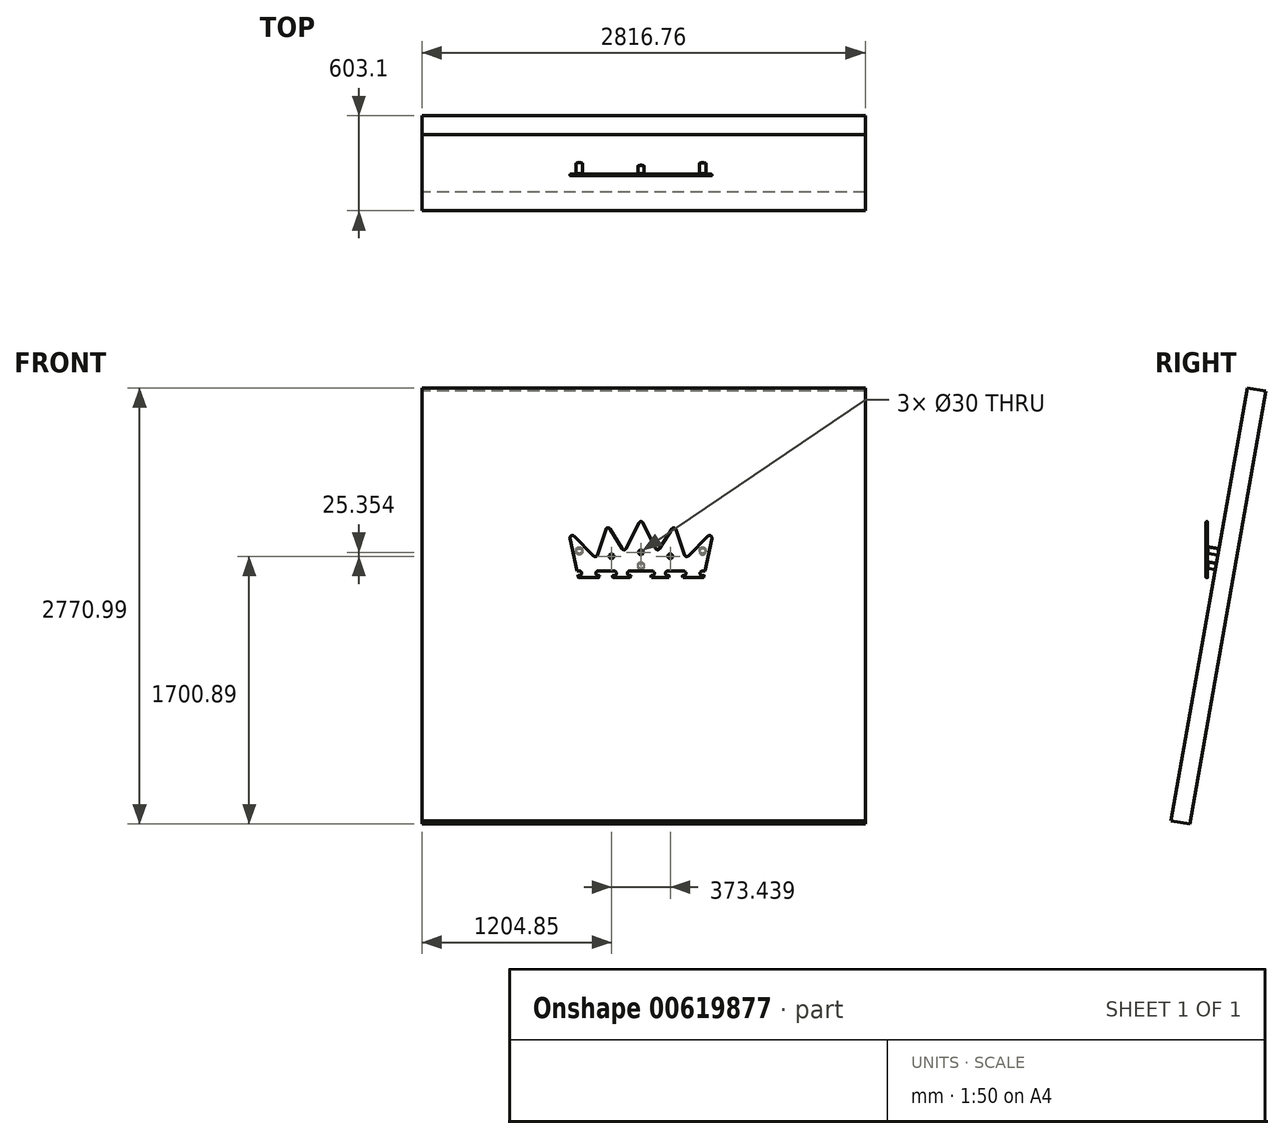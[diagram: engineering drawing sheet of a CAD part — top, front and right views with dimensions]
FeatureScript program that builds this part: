
annotation { "Feature Type Name" : "Feature", "Feature Type Description" : "" }
export const myFeature = defineFeature(function(context is Context, id is Id, definition is map)
    precondition{}
    {
        {
            var Q0;
            Q0=qCreatedBy(makeId("Front.planeOp"),FACE);
            var sketch = newSketch(context, id + "F0", { "sketchPlane" : qUnion([Q0])});
            skLineSegment(sketch, "E0.left", {"start": v(0, 0) * mm, "end": v(0, 300) * mm, "construction": true});
            skLineSegment(sketch, "E1", {"start": v(0, 0) * mm, "end": v(-52.87, 249.42) * mm});
            skLineSegment(sketch, "E2", {"start": v(-27.53, 263.07) * mm, "end": v(113.33, 120.6) * mm});
            skLineSegment(sketch, "E3", {"start": v(0, 35) * mm, "end": v(1158.58, 35) * mm, "construction": true});
            skArc(sketch, "E4.filletArc", {"start": v(-27.53, 263.07) * mm, "mid": v(-45.3, 265.73) * mm, "end": v(-52.87, 249.42) * mm});
            skLineSegment(sketch, "E5", {"start": v(397.13, 374.35) * mm, "end": v(397.13, 0) * mm});
            skLineSegment(sketch, "E6", {"start": v(0, 0) * mm, "end": v(397.13, 0) * mm});
            skLineSegment(sketch, "E7", {"start": v(113.33, 120.6) * mm, "end": v(184.19, 337.1) * mm});
            skLineSegment(sketch, "E8", {"start": v(184.19, 337.1) * mm, "end": v(291.92, 160.57) * mm});
            skLineSegment(sketch, "E9", {"start": v(291.92, 160.57) * mm, "end": v(397.13, 374.35) * mm});
            skSolve(sketch);
        }
        {
            var Q0;
            Q0=makeQuery(id+"F0.imprint","IMPRINT",FACE,{"disambiguationData":[TD([[makeQuery(id+"F0.imprint","IMPRINT",EDGE,{"derivedFrom":sQuery(id+"F0.wireOp",EDGE,"E1")}),-1.0]])]});
            extrude(context, id + "F1", {"entities" : qUnion([Q0]), "depth" : 9 * mm, "offsetDistance" : 25 * mm});
        }
        {
            var Q0;
            Q0=makeQuery(id+"F1.opExtrude","SWEPT_EDGE",EDGE,{"disambiguationData":[OSD([sQuery(id+"F0.wireOp",EDGE,"E2"),sQuery(id+"F0.wireOp",EDGE,"E7")])]});
            var Q1;
            Q1=makeQuery(id+"F1.opExtrude","SWEPT_EDGE",EDGE,{"disambiguationData":[OSD([sQuery(id+"F0.wireOp",EDGE,"E7"),sQuery(id+"F0.wireOp",EDGE,"E8")])]});
            var Q2;
            Q2=makeQuery(id+"F1.opExtrude","SWEPT_EDGE",EDGE,{"disambiguationData":[OSD([sQuery(id+"F0.wireOp",EDGE,"E8"),sQuery(id+"F0.wireOp",EDGE,"E9")])]});
            fillet(context, id + "F2", {"entities" : qUnion([Q0, Q1, Q2]), "radius" : 15 * mm, "tangentPropagation" : true, "allowEdgeOverflow" : false});
        }
        {
            var Q0;
            Q0=makeQuery(id+"F1.opExtrude","CAP_FACE",FACE,{"disambiguationData":[OSD([sQuery(id+"F0.wireOp",EDGE,"E1"),sQuery(id+"F0.wireOp",EDGE,"E2"),sQuery(id+"F0.wireOp",EDGE,"E4.filletArc"),sQuery(id+"F0.wireOp",EDGE,"E5"),sQuery(id+"F0.wireOp",EDGE,"E6"),sQuery(id+"F0.wireOp",EDGE,"E7"),sQuery(id+"F0.wireOp",EDGE,"E8"),sQuery(id+"F0.wireOp",EDGE,"E9")])],"isStart":false});
            var sketch = newSketch(context, id + "F3", { "sketchPlane" : qUnion([Q0])});
            skCircle(sketch, "E10", {"center": v(6.24, 27) * mm, "radius": 15 * mm});
            skLineSegment(sketch, "E11", {"start": v(6.24, 42) * mm, "end": v(-8.9, 42) * mm});
            skSolve(sketch);
        }
        {
            var Q0;
            {var subQ0=sQuery(id+"F3.wireOp",EDGE,"E10");var subQ1=makeQuery(id+"F3.imprint","INTERSECT",VERTEX,{"derivedFrom":[subQ0,sQuery(id+"F3.wireOp",EDGE,"E11")]});Q0=makeQuery(id+"F3.imprint","IMPRINT",FACE,{"disambiguationData":[TD([[makeQuery(id+"F3.imprint","IMPRINT",EDGE,{"disambiguationData":[TD([[subQ1,-1.0]])],"derivedFrom":subQ0}),1.0]])]});}
            var Q1;
            {var subQ0=sQuery(id+"F3.wireOp",EDGE,"E11");Q1=makeQuery(id+"F3.imprint","IMPRINT",FACE,{"disambiguationData":[TD([[makeQuery(id+"F3.imprint","IMPRINT",EDGE,{"derivedFrom":subQ0}),1.0]])]});}
            extrude(context, id + "F4", {"entities" : qUnion([Q0, Q1]), "operationType" : NewBodyOperationType.REMOVE, "endBound" : BoundingType.THROUGH_ALL, "oppositeDirection" : true, "depth" : 25 * mm, "offsetDistance" : 25 * mm});
        }
        {
            var Q0;
            Q0=makeQuery(id+"F1.opExtrude","CAP_FACE",FACE,{"disambiguationData":[OSD([sQuery(id+"F0.wireOp",EDGE,"E1"),sQuery(id+"F0.wireOp",EDGE,"E2"),sQuery(id+"F0.wireOp",EDGE,"E4.filletArc"),sQuery(id+"F0.wireOp",EDGE,"E5"),sQuery(id+"F0.wireOp",EDGE,"E6"),sQuery(id+"F0.wireOp",EDGE,"E7"),sQuery(id+"F0.wireOp",EDGE,"E8"),sQuery(id+"F0.wireOp",EDGE,"E9")])],"isStart":false});
            var sketch = newSketch(context, id + "F5", { "sketchPlane" : qUnion([Q0])});
            skCircle(sketch, "E12", {"center": v(126.24, 27) * mm, "radius": 15 * mm});
            skLineSegment(sketch, "E13", {"start": v(6.24, 27) * mm, "end": v(126.24, 27) * mm, "construction": true});
            skCircle(sketch, "E14.1.0.0", {"center": v(226.24, 27) * mm, "radius": 15 * mm});
            skCircle(sketch, "E14.2.0.0", {"center": v(326.24, 27) * mm, "radius": 15 * mm});
            skLineSegment(sketch, "E14.direction1", {"start": v(126.24, 27) * mm, "end": v(226.24, 27) * mm, "construction": true});
            skLineSegment(sketch, "E15", {"start": v(126.24, 42) * mm, "end": v(226.24, 42) * mm});
            skLineSegment(sketch, "E16", {"start": v(-3.26, 15.4) * mm, "end": v(135.75, 15.4) * mm, "construction": true});
            skLineSegment(sketch, "E17", {"start": v(135.75, 15.4) * mm, "end": v(216.74, 15.4) * mm, "construction": true});
            skLineSegment(sketch, "E18", {"start": v(326.24, 42) * mm, "end": v(397.13, 42) * mm});
            skLineSegment(sketch, "E19", {"start": v(335.75, 15.4) * mm, "end": v(397.13, 16.4) * mm, "construction": true});
            skLineSegment(sketch, "E20", {"start": v(135.75, 15.4) * mm, "end": v(129.34, 0) * mm});
            skLineSegment(sketch, "E21", {"start": v(216.74, 15.4) * mm, "end": v(220, 0) * mm});
            skLineSegment(sketch, "E22", {"start": v(335.75, 15.4) * mm, "end": v(329.34, 0) * mm});
            skSolve(sketch);
        }
        {
            var Q0;
            {var subQ0=sQuery(id+"F5.wireOp",EDGE,"E12");var subQ1=makeQuery(id+"F5.imprint","INTERSECT",VERTEX,{"derivedFrom":[subQ0,sQuery(id+"F5.wireOp",EDGE,"E15")]});Q0=makeQuery(id+"F5.imprint","IMPRINT",FACE,{"disambiguationData":[TD([[makeQuery(id+"F5.imprint","IMPRINT",EDGE,{"disambiguationData":[TD([[subQ1,-1.0]])],"derivedFrom":subQ0}),1.0]])]});}
            var Q1;
            {var subQ1=sQuery(id+"F5.wireOp",EDGE,"E15");Q1=makeQuery(id+"F5.imprint","IMPRINT",FACE,{"disambiguationData":[TD([[makeQuery(id+"F5.imprint","IMPRINT",EDGE,{"derivedFrom":subQ1}),-1.0]])]});}
            var Q2;
            {var subQ0=sQuery(id+"F5.wireOp",EDGE,"E14.1.0.0");var subQ1=makeQuery(id+"F5.imprint","INTERSECT",VERTEX,{"derivedFrom":[subQ0,sQuery(id+"F5.wireOp",EDGE,"E15")]});Q2=makeQuery(id+"F5.imprint","IMPRINT",FACE,{"disambiguationData":[TD([[makeQuery(id+"F5.imprint","IMPRINT",EDGE,{"disambiguationData":[TD([[subQ1,-1.0]])],"derivedFrom":subQ0}),1.0]])]});}
            var Q3;
            {var subQ0=sQuery(id+"F5.wireOp",EDGE,"E14.2.0.0");var subQ1=makeQuery(id+"F5.imprint","INTERSECT",VERTEX,{"derivedFrom":[subQ0,sQuery(id+"F5.wireOp",EDGE,"E18")]});Q3=makeQuery(id+"F5.imprint","IMPRINT",FACE,{"disambiguationData":[TD([[makeQuery(id+"F5.imprint","IMPRINT",EDGE,{"disambiguationData":[TD([[subQ1,-1.0]])],"derivedFrom":subQ0}),1.0]])]});}
            var Q4;
            {var subQ3=sQuery(id+"F5.wireOp",EDGE,"E18");Q4=makeQuery(id+"F5.imprint","IMPRINT",FACE,{"disambiguationData":[TD([[makeQuery(id+"F5.imprint","IMPRINT",EDGE,{"derivedFrom":subQ3}),-1.0]])]});}
            extrude(context, id + "F6", {"entities" : qUnion([Q0, Q1, Q2, Q3, Q4]), "operationType" : NewBodyOperationType.REMOVE, "endBound" : BoundingType.THROUGH_ALL, "oppositeDirection" : true, "depth" : 25 * mm, "offsetDistance" : 25 * mm});
        }
        {
            var Q0;
            Q0=makeQuery(id+"F4.boolean.opBoolean","COPY",EDGE,{"derivedFrom":makeQuery(id+"F4.opExtrude","SWEPT_EDGE",EDGE,{"disambiguationData":[OSD([sQuery(id+"F0.wireOp",EDGE,"E1"),sQuery(id+"F3.wireOp",EDGE,"E10")])]})});
            var Q1;
            Q1=makeQuery(id+"F1.opExtrude","SWEPT_EDGE",EDGE,{"disambiguationData":[OSD([sQuery(id+"F0.wireOp",EDGE,"E1"),sQuery(id+"F0.wireOp",EDGE,"E6")])]});
            var Q2;
            Q2=makeQuery(id+"F6.boolean.opBoolean","COPY",EDGE,{"derivedFrom":makeQuery(id+"F6.opExtrude","SWEPT_EDGE",EDGE,{"disambiguationData":[OSD([sQuery(id+"F5.wireOp",EDGE,"E12"),sQuery(id+"F5.wireOp",EDGE,"E20")])]})});
            var Q3;
            Q3=makeQuery(id+"F6.boolean.opBoolean","COPY",EDGE,{"derivedFrom":makeQuery(id+"F6.opExtrude","SWEPT_EDGE",EDGE,{"disambiguationData":[OSD([sQuery(id+"F0.wireOp",EDGE,"E6"),sQuery(id+"F5.wireOp",EDGE,"E20")])]})});
            var Q4;
            Q4=makeQuery(id+"F6.boolean.opBoolean","COPY",EDGE,{"derivedFrom":makeQuery(id+"F6.opExtrude","SWEPT_EDGE",EDGE,{"disambiguationData":[OSD([sQuery(id+"F5.wireOp",EDGE,"E14.2.0.0"),sQuery(id+"F5.wireOp",EDGE,"E22")])]})});
            var Q5;
            Q5=makeQuery(id+"F6.boolean.opBoolean","COPY",EDGE,{"derivedFrom":makeQuery(id+"F6.opExtrude","SWEPT_EDGE",EDGE,{"disambiguationData":[OSD([sQuery(id+"F0.wireOp",EDGE,"E6"),sQuery(id+"F5.wireOp",EDGE,"E22")])]})});
            var Q6;
            Q6=makeQuery(id+"F6.boolean.opBoolean","COPY",EDGE,{"derivedFrom":makeQuery(id+"F6.opExtrude","SWEPT_EDGE",EDGE,{"disambiguationData":[OSD([sQuery(id+"F0.wireOp",EDGE,"E6"),sQuery(id+"F5.wireOp",EDGE,"E21")])]})});
            var Q7;
            Q7=makeQuery(id+"F6.boolean.opBoolean","COPY",EDGE,{"derivedFrom":makeQuery(id+"F6.opExtrude","SWEPT_EDGE",EDGE,{"disambiguationData":[OSD([sQuery(id+"F5.wireOp",EDGE,"E14.1.0.0"),sQuery(id+"F5.wireOp",EDGE,"E21")])]})});
            fillet(context, id + "F7", {"entities" : qUnion([Q0, Q1, Q2, Q3, Q4, Q5, Q6, Q7]), "radius" : 2 * mm, "tangentPropagation" : true, "allowEdgeOverflow" : false});
        }
        {
            var Q0;
            Q0=makeQuery(id+"F1.opExtrude","CAP_FACE",FACE,{"disambiguationData":[OSD([sQuery(id+"F0.wireOp",EDGE,"E1"),sQuery(id+"F0.wireOp",EDGE,"E2"),sQuery(id+"F0.wireOp",EDGE,"E4.filletArc"),sQuery(id+"F0.wireOp",EDGE,"E5"),sQuery(id+"F0.wireOp",EDGE,"E6"),sQuery(id+"F0.wireOp",EDGE,"E7"),sQuery(id+"F0.wireOp",EDGE,"E8"),sQuery(id+"F0.wireOp",EDGE,"E9")])],"isStart":false});
            var sketch = newSketch(context, id + "F8", { "sketchPlane" : qUnion([Q0])});
            skCircle(sketch, "E23", {"center": v(210.41, 135.31) * mm, "radius": 15 * mm});
            skCircle(sketch, "E24", {"center": v(397.13, 160.66) * mm, "radius": 15 * mm});
            skSolve(sketch);
        }
        {
            var Q0;
            Q0=makeQuery(id+"F8.imprint","IMPRINT",FACE,{"disambiguationData":[TD([[makeQuery(id+"F8.imprint","IMPRINT",EDGE,{"derivedFrom":sQuery(id+"F8.wireOp",EDGE,"40AQ9wcr-OVRQ-jtMO-fQ6l-KvRctUFFu5MA")}),1.0]])]});
            var Q1;
            Q1=makeQuery(id+"F8.imprint","IMPRINT",FACE,{"disambiguationData":[TD([[makeQuery(id+"F8.imprint","IMPRINT",EDGE,{"derivedFrom":sQuery(id+"F8.wireOp",EDGE,"E23")}),1.0]])]});
            var Q2;
            {var subQ0=sQuery(id+"F8.wireOp",EDGE,"E24");var subQ1=makeQuery(id+"F1.opExtrude","CAP_EDGE",EDGE,{"disambiguationData":[OSD([sQuery(id+"F0.wireOp",EDGE,"E5")])],"isStart":false});var subQ2=makeQuery(id+"F8.imprint","INTERSECT",VERTEX,{"disambiguationData":[OD(0.0)],"derivedFrom":[subQ1,subQ0]});Q2=makeQuery(id+"F8.imprint","IMPRINT",FACE,{"disambiguationData":[TD([[makeQuery(id+"F8.imprint","IMPRINT",EDGE,{"disambiguationData":[TD([[subQ2,-1.0]])],"derivedFrom":subQ0}),1.0]])]});}
            extrude(context, id + "F9", {"entities" : qUnion([Q0, Q1, Q2]), "operationType" : NewBodyOperationType.REMOVE, "endBound" : BoundingType.THROUGH_ALL, "oppositeDirection" : true, "depth" : 25 * mm, "offsetDistance" : 25 * mm});
        }
        {
            var Q0;
            {var subQ0=sQuery(id+"F0.wireOp",EDGE,"E6");Q0=makeQuery(id+"F6.boolean.opBoolean","SPLIT",EDGE,{"disambiguationData":[TD([makeQuery(id+"F6.opExtrude","SWEPT_FACE",FACE,{"disambiguationData":[OSD([sQuery(id+"F5.wireOp",EDGE,"E21")])]})])],"derivedFrom":makeQuery(id+"F1.opExtrude","CAP_EDGE",EDGE,{"disambiguationData":[OSD([subQ0])],"isStart":true})});}
            cPlane(context, id + "F10", {"entities" : qUnion([Q0]), "cplaneType" : CPlaneType.LINE_ANGLE, "offset" : 25 * mm, "angle" : 10 * degree, "oppositeDirection" : true, "width" : 150 * mm, "height" : 150 * mm});
        }
        {
            var Q0;
            Q0=qCreatedBy(id+"F10.planeOp",FACE);
            cPlane(context, id + "F11", {"entities" : qUnion([Q0]), "cplaneType" : CPlaneType.OFFSET, "offset" : 40 * mm, "width" : 150 * mm, "height" : 150 * mm});
        }
        {
            var Q0;
            Q0=qCreatedBy(id+"F11.planeOp",FACE);
            var sketch = newSketch(context, id + "F12", { "sketchPlane" : qUnion([Q0])});
            skCircle(sketch, "E25", {"center": v(-5.4, 172.6) * mm, "radius": 20 * mm});
            skCircle(sketch, "E26", {"center": v(-397.13, 78.47) * mm, "radius": 20 * mm});
            skSolve(sketch);
        }
        {
            var Q0;
            Q0=makeQuery(id+"F12.imprint","IMPRINT",FACE,{"disambiguationData":[TD([[makeQuery(id+"F12.imprint","IMPRINT",EDGE,{"derivedFrom":sQuery(id+"F12.wireOp",EDGE,"E26")}),1.0]])]});
            var Q1;
            Q1=makeQuery(id+"F12.imprint","IMPRINT",FACE,{"disambiguationData":[TD([[makeQuery(id+"F12.imprint","IMPRINT",EDGE,{"derivedFrom":sQuery(id+"F12.wireOp",EDGE,"E25")}),1.0]])]});
            var Q2;
            {var subQ0=makeQuery(id+"F1.opExtrude","CAP_FACE",FACE,{"disambiguationData":[OSD([sQuery(id+"F0.wireOp",EDGE,"E1"),sQuery(id+"F0.wireOp",EDGE,"E2"),sQuery(id+"F0.wireOp",EDGE,"E4.filletArc"),sQuery(id+"F0.wireOp",EDGE,"E5"),sQuery(id+"F0.wireOp",EDGE,"E6"),sQuery(id+"F0.wireOp",EDGE,"E7"),sQuery(id+"F0.wireOp",EDGE,"E8"),sQuery(id+"F0.wireOp",EDGE,"E9")])],"isStart":true});Q2=makeQuery(id+"F15.boolean.opBoolean","MERGE",FACE,{"derivedFrom":[subQ0,makeQuery(id+"F15.opPattern","COPY",FACE,{"derivedFrom":subQ0,"instanceName":"1"})]});}
            extrude(context, id + "F13", {"entities" : qUnion([Q0, Q1]), "endBound" : BoundingType.UP_TO_SURFACE, "oppositeDirection" : true, "depth" : 25 * mm, "endBoundEntityFace" : qUnion([Q2]), "offsetDistance" : 25 * mm});
        }
        {
            var Q0;
            Q0=makeQuery(id+"F13.opExtrude","SWEPT_BODY",BODY,{"disambiguationData":[OSD([sQuery(id+"F12.wireOp",EDGE,"E25")])]});
            var Q1;
            {var subQ0=sQuery(id+"F0.wireOp",EDGE,"E9");var subQ4=sQuery(id+"F0.wireOp",EDGE,"E5");Q1=makeQuery(id+"F9.boolean.opBoolean","SPLIT",FACE,{"disambiguationData":[TD([makeQuery(id+"F1.opExtrude","SWEPT_FACE",FACE,{"disambiguationData":[OSD([subQ0])]})])],"derivedFrom":makeQuery(id+"F1.opExtrude","SWEPT_FACE",FACE,{"disambiguationData":[OSD([subQ4])]})});}
            mirror(context, id + "F14", {"entities" : qUnion([Q0]), "mirrorPlane" : qUnion([Q1])});
        }
        {
            var Q0;
            Q0=makeQuery(id+"F1.opExtrude","SWEPT_BODY",BODY,{"disambiguationData":[OSD([sQuery(id+"F0.wireOp",EDGE,"E1"),sQuery(id+"F0.wireOp",EDGE,"E2"),sQuery(id+"F0.wireOp",EDGE,"E4.filletArc"),sQuery(id+"F0.wireOp",EDGE,"E5"),sQuery(id+"F0.wireOp",EDGE,"E6"),sQuery(id+"F0.wireOp",EDGE,"E7"),sQuery(id+"F0.wireOp",EDGE,"E8"),sQuery(id+"F0.wireOp",EDGE,"E9")])]});
            var Q1;
            Q1=makeQuery(id+"F1.opExtrude","SWEPT_FACE",FACE,{"disambiguationData":[OSD([sQuery(id+"F0.wireOp",EDGE,"E5")])]});
            mirror(context, id + "F15", {"operationType" : NewBodyOperationType.ADD, "entities" : qUnion([Q0]), "mirrorPlane" : qUnion([Q1])});
        }
        {
            var Q0;
            {var subQ0=makeQuery(id+"F1.opExtrude","SWEPT_EDGE",EDGE,{"disambiguationData":[OSD([sQuery(id+"F0.wireOp",EDGE,"E5"),sQuery(id+"F0.wireOp",EDGE,"E9")])]});Q0=makeQuery(id+"F15.boolean.opBoolean","MERGE",EDGE,{"derivedFrom":[subQ0,makeQuery(id+"F15.opPattern","COPY",EDGE,{"derivedFrom":subQ0,"instanceName":"1"})]});}
            fillet(context, id + "F16", {"entities" : qUnion([Q0]), "radius" : 15 * mm, "tangentPropagation" : true, "allowEdgeOverflow" : false});
        }
        {
            var Q0;
            Q0=qCreatedBy(id+"F11.planeOp",FACE);
            var sketch = newSketch(context, id + "F17", { "sketchPlane" : qUnion([Q0])});
            skLineSegment(sketch, "E27.bottom", {"start": v(-1822.32, 1231.06) * mm, "end": v(994.44, 1231.06) * mm});
            skLineSegment(sketch, "E27.top", {"start": v(-1822.32, -1561.52) * mm, "end": v(994.44, -1561.52) * mm});
            skLineSegment(sketch, "E27.left", {"start": v(-1822.32, 1231.06) * mm, "end": v(-1822.32, -1561.52) * mm});
            skLineSegment(sketch, "E27.right", {"start": v(994.44, 1231.06) * mm, "end": v(994.44, -1561.52) * mm});
            skSolve(sketch);
        }
        {
            var Q0;
            Q0=makeQuery(id+"F17.imprint","IMPRINT",FACE,{"disambiguationData":[TD([[makeQuery(id+"F17.imprint","IMPRINT",EDGE,{"derivedFrom":sQuery(id+"F17.wireOp",EDGE,"E27.bottom")}),-1.0]])]});
            extrude(context, id + "F18", {"entities" : qUnion([Q0]), "depth" : 120 * mm, "offsetDistance" : 25 * mm});
        }
        {
            var Q0;
            {var subQ0=makeQuery(id+"F1.opExtrude","CAP_FACE",FACE,{"disambiguationData":[OSD([sQuery(id+"F0.wireOp",EDGE,"E1"),sQuery(id+"F0.wireOp",EDGE,"E2"),sQuery(id+"F0.wireOp",EDGE,"E4.filletArc"),sQuery(id+"F0.wireOp",EDGE,"E5"),sQuery(id+"F0.wireOp",EDGE,"E6"),sQuery(id+"F0.wireOp",EDGE,"E7"),sQuery(id+"F0.wireOp",EDGE,"E8"),sQuery(id+"F0.wireOp",EDGE,"E9")])],"isStart":false});Q0=makeQuery(id+"F15.boolean.opBoolean","MERGE",FACE,{"derivedFrom":[subQ0,makeQuery(id+"F15.opPattern","COPY",FACE,{"derivedFrom":subQ0,"instanceName":"1"})]});}
            fillet(context, id + "F19", {"entities" : qUnion([Q0]), "radius" : 3 * mm, "tangentPropagation" : true, "allowEdgeOverflow" : false});
        }
        {
            var Q0;
            {var subQ0=makeQuery(id+"F1.opExtrude","CAP_FACE",FACE,{"disambiguationData":[OSD([sQuery(id+"F0.wireOp",EDGE,"E1"),sQuery(id+"F0.wireOp",EDGE,"E2"),sQuery(id+"F0.wireOp",EDGE,"E4.filletArc"),sQuery(id+"F0.wireOp",EDGE,"E5"),sQuery(id+"F0.wireOp",EDGE,"E6"),sQuery(id+"F0.wireOp",EDGE,"E7"),sQuery(id+"F0.wireOp",EDGE,"E8"),sQuery(id+"F0.wireOp",EDGE,"E9")])],"isStart":true});Q0=makeQuery(id+"F15.boolean.opBoolean","MERGE",FACE,{"derivedFrom":[subQ0,makeQuery(id+"F15.opPattern","COPY",FACE,{"derivedFrom":subQ0,"instanceName":"1"})]});}
            fillet(context, id + "F20", {"entities" : qUnion([Q0]), "radius" : 3 * mm, "tangentPropagation" : true, "allowEdgeOverflow" : false});
        }
    });
